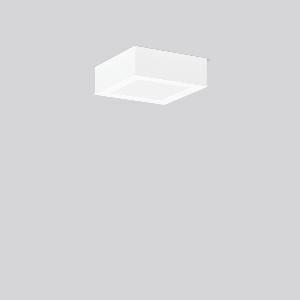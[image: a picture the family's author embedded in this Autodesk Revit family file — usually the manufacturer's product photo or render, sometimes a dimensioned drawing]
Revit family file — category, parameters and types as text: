
# Revit family: toledo_flat_square_a_672267_002_1_89_49e9
name_source: partatom
category: Lighting Fixtures
units: mm (PartAtom-declared; Revit-internal decimal feet)

## family parameters
Cut with Voids When Loaded = No
Host = Face
Light Source = No
Part Type = Normal
Room Calculation Point = No
Round Connector Dimension = Use Diameter
Shared = No

## types (1)
- TOLEDO FLAT square A (1 x LED Modul 840, 730 lm, 4000)
    Apparent Load = 9 VA
    CIE Flux Codes = 49 80 96 100 100
    Color Rendering = 80
    Color Temperature = 4000
    Default Elevation = 1800 mm
    Description = Series: TOLEDO FLAT square
Ultra thin surface mounted downlight. For escape route illumination. Surface mounted housing: sheet steel, powder-coated. Square cover plate: die-cast aluminium, powder coated. Light guide and diffuser made of non-yellowing PMMA, opal matt. Driver integrated. Suitable for connection to central battery systems. With AC Control monitoring module for LUXIFAIR central battery units. 
Colour: white
Length: 172 mm
Width: 172 mm
Height: 58 mm
Weight: 1.38 kg
Operating mode: maintained power mode
Lamp: LED
Socket: without socket
Colour temperature: 4000K
Colour rendering index (CRI): 80
System power: 9 W
Rated luminous flux: 730 lm
Luminous flux, emergency: 730 lm
System power, emergency: 9 W
Control gear: Regulated power supply
Protection class: I
Type of protection: IP 40
    Height = 58 mm
    Lamp = 1 x LED Modul 840
    Lamp Light Flux = 730 lm
    Lamp count = 1
    Length = 172 mm
    Lifetime = 50000 h
    Luminous efficacy = 81 lm/W
    Manufacturer = RZB
    ModVariant = No
    Model = 672267.002.1.89
    Mounting Place = Ceiling
    Mounting Type = Surface mounted
    Number of Poles = 1
    OnlyDefault = Yes
    Power Factor = 1
    Product Name = TOLEDO FLAT square A
    Product group = Surface mounted downlights
    ProductGroupID = 302
    Protection Class = Protection class I
    Protection Degree = IP 40
    RLX_Detail_Level = 1
    RLX_Emergency_Light_Flux = 730 lm
    RLX_Emergency_Type = 3
    RLX_Emergency_Type_DB = Yes
    RlxData = <blob elided: 14337 chars, md5=ad8d1843>
    Socket = socket
    Standby Power = 0 W
    System Light Flux = 730 lm
    System Power = 9 W
    Type Comments = Product without accessories
    Type Image = 901552.002.jpg
    URL = http://relux.com
    VarID = ---
    Voltage = 230 V
    Voltage Range = 220-240 V
    Weight = 0.00 kg
    Width = 172 mm

## geometry (parser evidence)
native form markers: Sweep x11
no freeform markers — native parametric forms only
